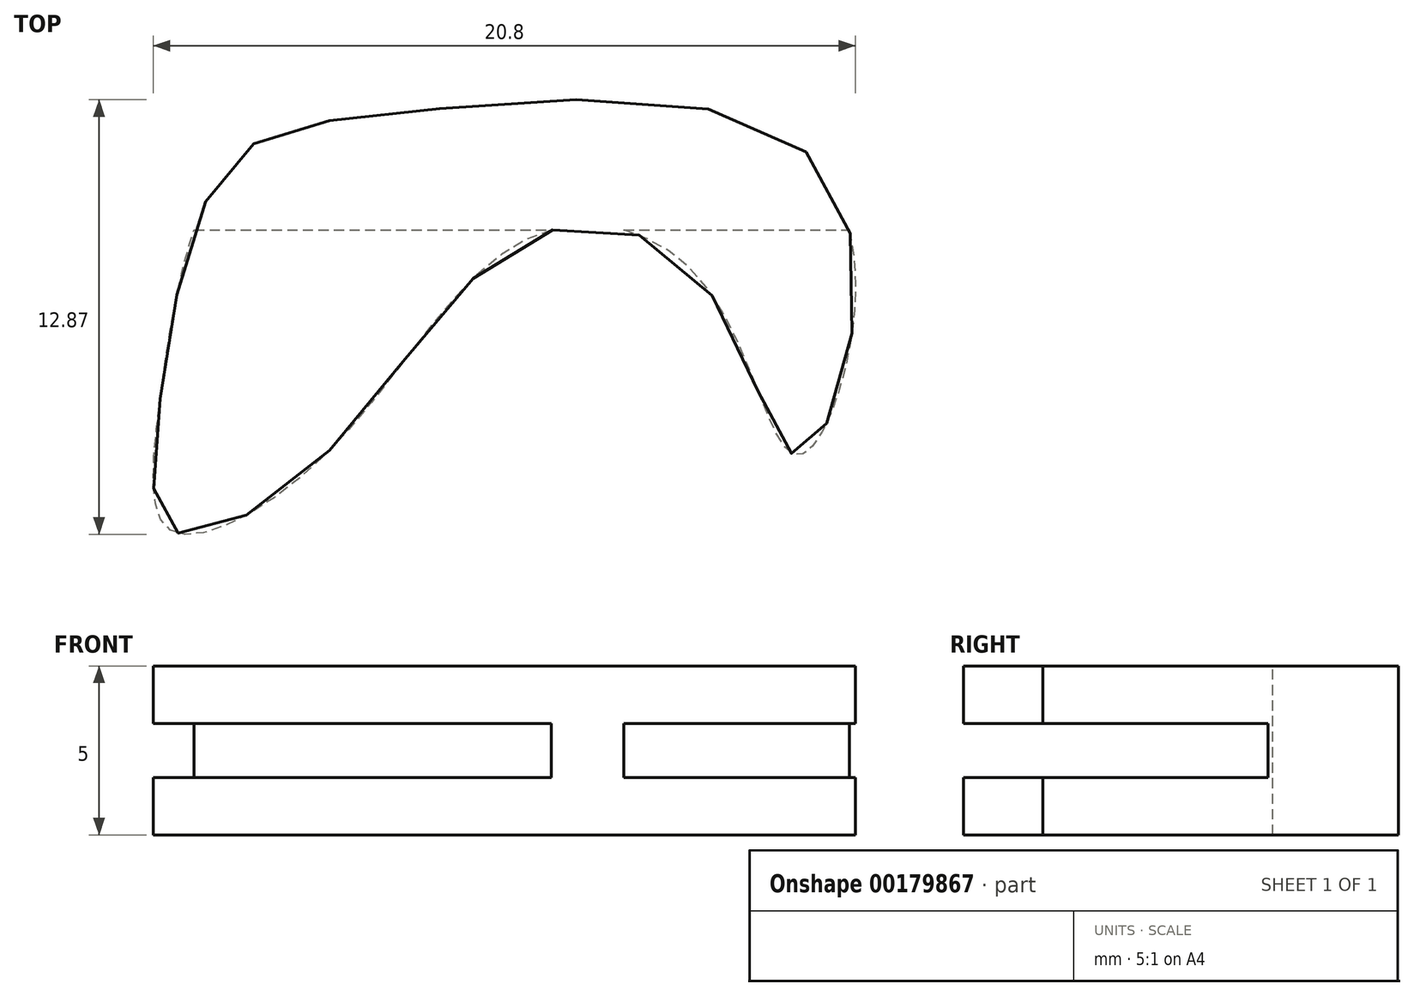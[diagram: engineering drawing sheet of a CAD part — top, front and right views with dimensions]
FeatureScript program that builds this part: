
annotation { "Feature Type Name" : "Feature", "Feature Type Description" : "" }
export const myFeature = defineFeature(function(context is Context, id is Id, definition is map)
    precondition{}
    {
        {
            var Q0;
            Q0=qCreatedBy(makeId("Top.planeOp"),FACE);
            var sketch = newSketch(context, id + "F0", { "sketchPlane" : qUnion([Q0])});
            skLineSegment(sketch, "E0", {"start": v(0, 0) * mm, "end": v(20, 0) * mm, "construction": true});
            skLineSegment(sketch, "E1", {"start": v(0, 0) * mm, "end": v(0, 10) * mm, "construction": true});
            skFitSpline(sketch, "E2", {"points": [v(0, 0) * mm, v(1.95, 6.83) * mm, v(6.8, 8.45) * mm, v(18.68, 7.66) * mm, v(20.4, 1.45) * mm, v(18.78, -1.65) * mm, v(16.09, 3.42) * mm, v(10.85, 4.73) * mm, v(4.84, -1.69) * mm, v(0.32, -3.9) * mm, v(0, 0) * mm]});
            skSolve(sketch);
        }
        {
            var Q0;
            Q0=makeQuery(id+"F0.imprint","IMPRINT",FACE,{"disambiguationData":[TD([[makeQuery(id+"F0.imprint","IMPRINT",EDGE,{"derivedFrom":sQuery(id+"F0.wireOp",EDGE,"E2")}),-1.0]])]});
            extrude(context, id + "F1", {"entities" : qUnion([Q0]), "depth" : 5 * mm});
        }
        {
            var Q0;
            Q0=qCreatedBy(makeId("Front.planeOp"),FACE);
            var sketch = newSketch(context, id + "F2", { "sketchPlane" : qUnion([Q0])});
            skLineSegment(sketch, "E3.0", {"start": v(-0.2, 5) * mm, "end": v(20.59, 5) * mm, "construction": true});
            skLineSegment(sketch, "E4.0", {"start": v(-0.2, 0) * mm, "end": v(20.59, 0) * mm, "construction": true});
            skLineSegment(sketch, "E5", {"start": v(-0.2, 5) * mm, "end": v(-0.2, 0) * mm, "construction": true});
            skLineSegment(sketch, "E6.bottom", {"start": v(-0.2, 2.5) * mm, "end": v(20.62, 2.5) * mm});
            skLineSegment(sketch, "E6.top", {"start": v(-0.2, 1.7) * mm, "end": v(20.62, 1.7) * mm});
            skLineSegment(sketch, "E6.left", {"start": v(-0.2, 2.5) * mm, "end": v(-0.2, 1.7) * mm});
            skLineSegment(sketch, "E6.right", {"start": v(20.62, 2.5) * mm, "end": v(20.62, 1.7) * mm});
            skLineSegment(sketch, "E7.MirrorCS", {"start": v(-0.2, 3.3) * mm, "end": v(20.62, 3.3) * mm});
            skLineSegment(sketch, "E8.MirrorCS", {"start": v(-0.2, 2.5) * mm, "end": v(-0.2, 3.3) * mm});
            skLineSegment(sketch, "E9.MirrorCS", {"start": v(20.62, 2.5) * mm, "end": v(20.62, 3.3) * mm});
            skSolve(sketch);
        }
        {
            var Q0;
            Q0 = qSketchRegion(id + "F2", true);
            extrude(context, id + "F3", {"entities" : qUnion([Q0]), "operationType" : NewBodyOperationType.REMOVE, "endBound" : BoundingType.SYMMETRIC, "oppositeDirection" : true, "depth" : 10 * mm});
        }
    });
